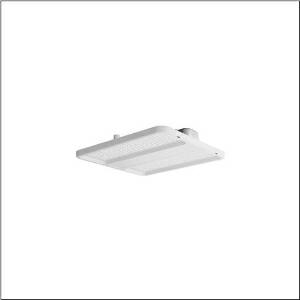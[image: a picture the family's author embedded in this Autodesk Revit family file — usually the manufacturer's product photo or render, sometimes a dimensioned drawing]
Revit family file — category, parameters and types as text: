
# Revit family: highbay_11_midi_51hn12da4eda
name_source: partatom
category: Lighting Fixtures
units: mm (PartAtom-declared; Revit-internal decimal feet)

## family parameters
Cut with Voids When Loaded = No
Host = Face
Light Source = No
Part Type = Normal
Room Calculation Point = No
Round Connector Dimension = Use Diameter
Shared = No

## types (1)
- --- (1 x LED, 1490 lm, 8.2 W, 4000K)
    Apparent Load = 8 VA
    CIE Flux Codes = 87 98 100 100 100
    Color Rendering = 80
    Color Temperature = 4000K
    Default Elevation = 1800 mm
    Description = high bay luminaire Highbay 11 midi; direct symmetric wide distribution, light control with lens of PMMA; UGR ≤ 19 (X = 4H | Y = 8H | S = 0.25H | reflection values 70/50/20); luminous flux: 10.000lm; light colour: 840, colour temperature: 4000K, MacAdam ≤ 2 SDCM (initial), colour rendering: CRI > 80; luminous efficacy: 209,6lm/W; rated service life: 100.000h (L95/B50) at AT= 25°C; control: DALI 2; housing frame of high-performance plastic PA6, matt traffic white (RAL 9016); cover of PMMA; dimension (LxWxH): 474 x 442 x 72mm; luminaire connection: terminal, 5-pole, max. 2.5mm² (cable entry for one cable, Ø 8.5..16mm); mains connection: 230..240V, AC/DC 0/50..60Hz; connected load: 47,7W; protection rating (complete): IP66; insulation class (complete): insulation class I (protective earthing); protection symbol: D; impact resistance: IK08; halogen-free wiring; for central battery installations according to DIN EN 60598-2-22; corresponds to IFS (International Featured Standards) requirements for safety and quality in the food industry; LABS conformity tested according to VDMA 24364:2018-05; certification: CE, ENEC, VDE, UKCA; permissible operating ambient temperature: -40..+70°C (reducing of maximum allowable ambient temperature of 5°C with ceiling mounting); packaging unit: 1 piece; (delivery without accessories; please order mounting accessories separately)
    Height = 72 mm  [stored 0.23622 ft]
    Lamp = 1 x LED
    Lamp Light Flux = 1490 lm
    Lamp Power = 8.2 W
    Lamp count = 1
    Length = 474 mm
    Luminous efficacy = 182 lm/W
    Manufacturer = Siteco
    ModVariant = No
    Model = 51HN12DA4EDA
    Mounting Place = Ceiling
    Mounting Type = Pendant
    Number of Poles = 1
    OnlyDefault = Yes
    Power Factor = 1
    Product Name = Highbay 11 midi
    Product group = high bay luminaire
    ProductGroupID = 901
    Protection Class = Protection class I
    Protection Degree = IP 66
    RLX_Detail_Level = 1
    RLX_Emergency_Light_Flux = 0 lm
    RLX_Emergency_Type = 0
    RLX_Emergency_Type_DB = No
    RlxData = <blob elided: 16629 chars, md5=437f978e>
    Socket = socket
    Standby Power = 0 W
    System Light Flux = 1490 lm
    System Power = 8 W
    Type Comments = : DC mode (central or group accumulator) initial emergency light level
    Type Image = l_1363240.jpg
    URL = http://relux.com
    VarID = @adj_005187
    Voltage = 0 V
    Weight = 0.00 kg
    Width = 442 mm

note: [stored X ft] marks values corroborated as IEEE doubles in the binary element streams (Revit-internal decimal feet)

## geometry (parser evidence)
native form markers: Blend x4, Sweep x11
no freeform markers — native parametric forms only
